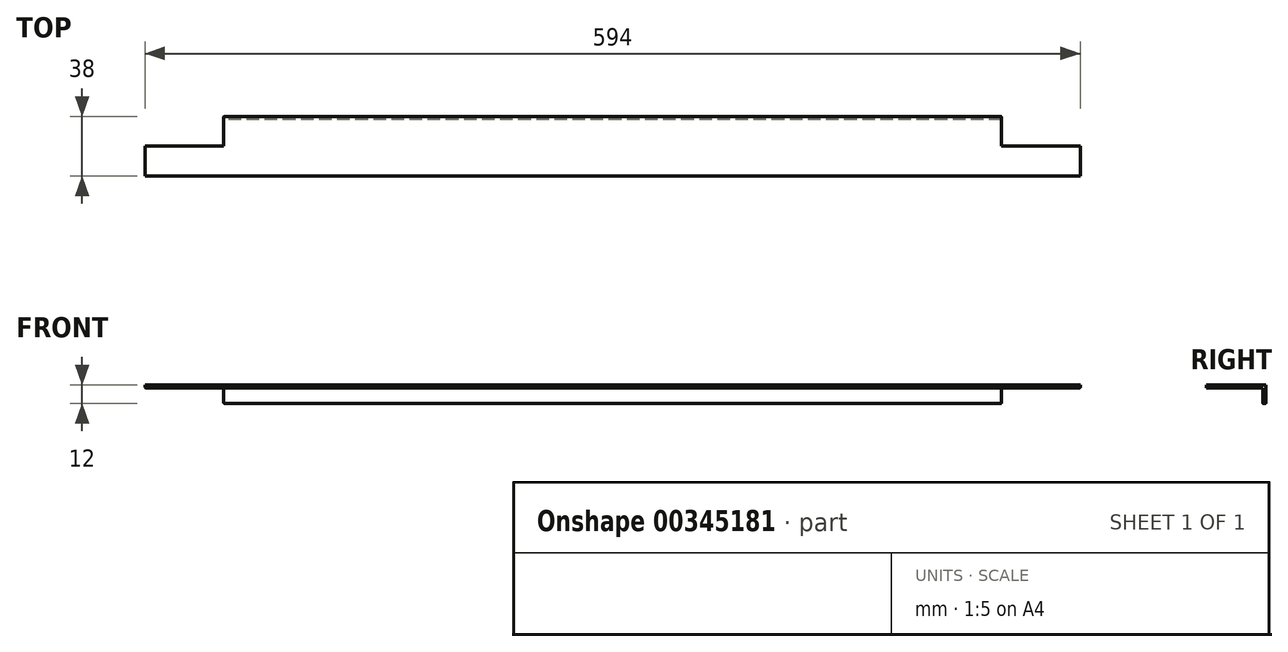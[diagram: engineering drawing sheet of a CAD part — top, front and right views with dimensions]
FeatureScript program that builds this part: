
annotation { "Feature Type Name" : "Feature", "Feature Type Description" : "" }
export const myFeature = defineFeature(function(context is Context, id is Id, definition is map)
    precondition{}
    {
        {
            var Q0;
            Q0=qCreatedBy(makeId("Front.planeOp"),FACE);
            var sketch = newSketch(context, id + "F0", { "sketchPlane" : qUnion([Q0])});
            skLineSegment(sketch, "E0.bottom", {"start": v(0, 0) * mm, "end": v(-51.96, 0) * mm});
            skLineSegment(sketch, "E0.top", {"start": v(0, 27.06) * mm, "end": v(-51.96, 27.06) * mm});
            skLineSegment(sketch, "E0.left", {"start": v(0, 0) * mm, "end": v(0, 27.06) * mm});
            skLineSegment(sketch, "E0.right", {"start": v(-51.96, 0) * mm, "end": v(-51.96, 27.06) * mm});
            skSolve(sketch);
        }
        {
            var Q0;
            Q0=makeQuery(id+"F0.imprint","IMPRINT",FACE,{"disambiguationData":[TD([[makeQuery(id+"F0.imprint","IMPRINT",EDGE,{"derivedFrom":sQuery(id+"F0.wireOp",EDGE,"E0.bottom")}),-1.0]])]});
            extrude(context, id + "F1", {"entities" : qUnion([Q0]), "oppositeDirection" : true, "depth" : 38 * mm});
        }
        {
            var Q0;
            Q0=makeQuery(id+"F1.opExtrude","SWEPT_FACE",FACE,{"disambiguationData":[OSD([sQuery(id+"F0.wireOp",EDGE,"E0.bottom")])]});
            extrude(context, id + "F2", {"entities" : qUnion([Q0]), "operationType" : NewBodyOperationType.INTERSECT, "oppositeDirection" : true, "depth" : 2 * mm});
        }
        {
            var Q0;
            Q0=makeQuery(id+"F1.opExtrude","SWEPT_FACE",FACE,{"disambiguationData":[OSD([sQuery(id+"F0.wireOp",EDGE,"E0.left")])]});
            extrude(context, id + "F3", {"entities" : qUnion([Q0]), "operationType" : NewBodyOperationType.ADD, "oppositeDirection" : true, "depth" : 594 * mm});
        }
        {
            var Q0;
            Q0=makeQuery(id+"F1.opExtrude","SWEPT_FACE",FACE,{"disambiguationData":[OSD([sQuery(id+"F0.wireOp",EDGE,"E0.left")])]});
            var sketch = newSketch(context, id + "F4", { "sketchPlane" : qUnion([Q0])});
            skLineSegment(sketch, "E1", {"start": v(19, 2) * mm, "end": v(19, 0) * mm});
            skSolve(sketch);
        }
        {
            var Q0;
            {var subQ0=sQuery(id+"F4.wireOp",EDGE,"E1");Q0=makeQuery(id+"F4.imprint","IMPRINT",FACE,{"disambiguationData":[TD([[makeQuery(id+"F4.imprint","IMPRINT",EDGE,{"derivedFrom":subQ0}),1.0]])]});}
            extrude(context, id + "F5", {"entities" : qUnion([Q0]), "operationType" : NewBodyOperationType.REMOVE, "oppositeDirection" : true, "depth" : 50 * mm});
        }
        {
            var Q0;
            Q0=makeQuery(id+"F3.opExtrude","CAP_FACE",FACE,{"disambiguationData":[OSD([sQuery(id+"F0.wireOp",EDGE,"E0.left")])],"isStart":false});
            var sketch = newSketch(context, id + "F6", { "sketchPlane" : qUnion([Q0])});
            skLineSegment(sketch, "E2", {"start": v(-19, 2) * mm, "end": v(-19, 0) * mm});
            skSolve(sketch);
        }
        {
            var Q0;
            {var subQ0=sQuery(id+"F6.wireOp",EDGE,"E2");Q0=makeQuery(id+"F6.imprint","IMPRINT",FACE,{"disambiguationData":[TD([[makeQuery(id+"F6.imprint","IMPRINT",EDGE,{"derivedFrom":subQ0}),-1.0]])]});}
            extrude(context, id + "F7", {"entities" : qUnion([Q0]), "operationType" : NewBodyOperationType.REMOVE, "oppositeDirection" : true, "depth" : 50 * mm});
        }
        {
            var Q0;
            {var subQ0=sQuery(id+"F0.wireOp",EDGE,"E0.left");var subQ1=sQuery(id+"F0.wireOp",EDGE,"E0.bottom");Q0=makeQuery(id+"F3.boolean.opBoolean","MERGE",FACE,{"derivedFrom":[makeQuery(id+"F1.opExtrude","SWEPT_FACE",FACE,{"disambiguationData":[OSD([subQ1])]}),makeQuery(id+"F3.opExtrude","SWEPT_FACE",FACE,{"disambiguationData":[OSD([subQ1,subQ0]),TDD([makeQuery(id+"F1.opExtrude","SWEPT_EDGE",EDGE,{"disambiguationData":[OSD([subQ1,subQ0])]})])]})]});}
            var sketch = newSketch(context, id + "F8", { "sketchPlane" : qUnion([Q0])});
            skLineSegment(sketch, "E3.bottom", {"start": v(-50, -38) * mm, "end": v(-544, -38) * mm});
            skLineSegment(sketch, "E3.top", {"start": v(-50, -28.5) * mm, "end": v(-544, -28.5) * mm});
            skLineSegment(sketch, "E3.left", {"start": v(-50, -38) * mm, "end": v(-50, -28.5) * mm});
            skLineSegment(sketch, "E3.right", {"start": v(-544, -38) * mm, "end": v(-544, -28.5) * mm});
            skSolve(sketch);
        }
        {
            var Q0;
            Q0=makeQuery(id+"F8.imprint","IMPRINT",FACE,{"disambiguationData":[TD([[makeQuery(id+"F8.imprint","IMPRINT",EDGE,{"derivedFrom":sQuery(id+"F8.wireOp",EDGE,"E3.bottom")}),-1.0]])]});
            extrude(context, id + "F9", {"entities" : qUnion([Q0]), "operationType" : NewBodyOperationType.ADD, "depth" : 10 * mm});
        }
        {
            var Q0;
            Q0=makeQuery(id+"F9.opExtrude","SWEPT_FACE",FACE,{"disambiguationData":[OSD([sQuery(id+"F8.wireOp",EDGE,"E3.top")])]});
            extrude(context, id + "F10", {"entities" : qUnion([Q0]), "operationType" : NewBodyOperationType.REMOVE, "oppositeDirection" : true, "depth" : 7.5 * mm});
        }
        {
            var Q0;
            {var subQ0=sQuery(id+"F0.wireOp",EDGE,"E0.left");var subQ1=sQuery(id+"F0.wireOp",EDGE,"E0.bottom");Q0=makeQuery(id+"F3.boolean.opBoolean","MERGE",EDGE,{"derivedFrom":[makeQuery(id+"F2.boolean.opBoolean","COPY",EDGE,{"derivedFrom":makeQuery(id+"F2.boolean.toolComplement.opBoolean","COPY",EDGE,{"derivedFrom":makeQuery(id+"F2.opExtrude","CAP_EDGE",EDGE,{"disambiguationData":[OSD([subQ1]),TDD([makeQuery(id+"F1.opExtrude","CAP_EDGE",EDGE,{"disambiguationData":[OSD([subQ1])],"isStart":false})])],"isStart":false})})}),makeQuery(id+"F3.opExtrude","SWEPT_EDGE",EDGE,{"disambiguationData":[OSD([subQ1,subQ0]),TDD([makeQuery(id+"F2.boolean.opBoolean","COPY",VERTEX,{"derivedFrom":makeQuery(id+"F2.boolean.toolComplement.opBoolean","COPY",VERTEX,{"derivedFrom":makeQuery(id+"F2.opExtrude","CAP_VERTEX",VERTEX,{"disambiguationData":[OSD([subQ1,subQ0]),TDD([makeQuery(id+"F1.opExtrude","CAP_VERTEX",VERTEX,{"disambiguationData":[OSD([subQ1,subQ0])],"isStart":false})])],"isStart":false})})})])]})]});}
            var Q1;
            Q1=makeQuery(id+"F9.boolean.opBoolean","MERGE",EDGE,{"derivedFrom":[makeQuery(id+"F7.boolean.opBoolean","COPY",EDGE,{"derivedFrom":makeQuery(id+"F7.opExtrude","CAP_EDGE",EDGE,{"disambiguationData":[OSD([sQuery(id+"F0.wireOp",EDGE,"E0.left")])],"isStart":false})}),makeQuery(id+"F9.opExtrude","SWEPT_EDGE",EDGE,{"disambiguationData":[OSD([sQuery(id+"F8.wireOp",EDGE,"E3.bottom"),sQuery(id+"F8.wireOp",EDGE,"E3.right")])]})]});
            var Q2;
            {var subQ0=sQuery(id+"F0.wireOp",EDGE,"E0.left");var subQ1=sQuery(id+"F0.wireOp",EDGE,"E0.bottom");var subQ2=makeQuery(id+"F3.opExtrude","CAP_EDGE",EDGE,{"disambiguationData":[OSD([subQ1,subQ0]),TDD([makeQuery(id+"F2.boolean.opBoolean","COPY",EDGE,{"derivedFrom":makeQuery(id+"F2.boolean.toolComplement.opBoolean","COPY",EDGE,{"derivedFrom":makeQuery(id+"F2.opExtrude","CAP_EDGE",EDGE,{"disambiguationData":[OSD([subQ1,subQ0])],"isStart":false})})})])],"isStart":false});Q2=makeQuery(id+"F7.boolean.opBoolean","COPY",EDGE,{"derivedFrom":makeQuery(id+"F7.opExtrude","CAP_EDGE",EDGE,{"disambiguationData":[OSD([subQ1,subQ0]),TDD([makeQuery(id+"F6.imprint","IMPRINT",EDGE,{"disambiguationData":[TD([[makeQuery(id+"F6.imprint","INTERSECT",VERTEX,{"derivedFrom":[subQ2,sQuery(id+"F6.wireOp",EDGE,"E2")]}),1.0]])],"derivedFrom":subQ2})])],"isStart":false})});}
            var Q3;
            {var subQ0=sQuery(id+"F8.wireOp",EDGE,"E3.right");var subQ1=sQuery(id+"F8.wireOp",EDGE,"E3.top");var subQ2=sQuery(id+"F0.wireOp",EDGE,"E0.left");var subQ3=sQuery(id+"F0.wireOp",EDGE,"E0.bottom");var subQ4=makeQuery(id+"F3.opExtrude","CAP_EDGE",EDGE,{"disambiguationData":[OSD([subQ3,subQ2]),TDD([makeQuery(id+"F1.opExtrude","SWEPT_EDGE",EDGE,{"disambiguationData":[OSD([subQ3,subQ2])]})])],"isStart":false});Q3=makeQuery(id+"F10.boolean.opBoolean","MERGE",EDGE,{"derivedFrom":[makeQuery(id+"F7.boolean.opBoolean","COPY",EDGE,{"derivedFrom":makeQuery(id+"F7.opExtrude","CAP_EDGE",EDGE,{"disambiguationData":[OSD([subQ3,subQ2]),TDD([makeQuery(id+"F6.imprint","IMPRINT",EDGE,{"disambiguationData":[TD([[makeQuery(id+"F6.imprint","INTERSECT",VERTEX,{"derivedFrom":[subQ4,sQuery(id+"F6.wireOp",EDGE,"E2")]}),1.0]])],"derivedFrom":subQ4})])],"isStart":false})}),makeQuery(id+"F10.opExtrude","SWEPT_EDGE",EDGE,{"disambiguationData":[OSD([subQ3,subQ2,subQ1,subQ0]),TDD([makeQuery(id+"F9.opExtrude","CAP_VERTEX",VERTEX,{"disambiguationData":[OSD([subQ3,subQ2,subQ1,subQ0])],"isStart":true})])]})]});}
            var Q4;
            Q4=makeQuery(id+"F10.boolean.opBoolean","COPY",EDGE,{"derivedFrom":makeQuery(id+"F10.opExtrude","CAP_EDGE",EDGE,{"disambiguationData":[OSD([sQuery(id+"F0.wireOp",EDGE,"E0.bottom"),sQuery(id+"F0.wireOp",EDGE,"E0.left"),sQuery(id+"F8.wireOp",EDGE,"E3.top"),sQuery(id+"F8.wireOp",EDGE,"E3.right")])],"isStart":false})});
            var Q5;
            {var subQ0=sQuery(id+"F0.wireOp",EDGE,"E0.left");var subQ1=sQuery(id+"F0.wireOp",EDGE,"E0.bottom");Q5=makeQuery(id+"F3.opExtrude","CAP_EDGE",EDGE,{"disambiguationData":[OSD([subQ1,subQ0]),TDD([makeQuery(id+"F2.boolean.opBoolean","COPY",EDGE,{"derivedFrom":makeQuery(id+"F2.boolean.toolComplement.opBoolean","COPY",EDGE,{"derivedFrom":makeQuery(id+"F2.opExtrude","CAP_EDGE",EDGE,{"disambiguationData":[OSD([subQ1,subQ0])],"isStart":false})})})])],"isStart":false});}
            var Q6;
            {var subQ0=sQuery(id+"F0.wireOp",EDGE,"E0.left");var subQ1=sQuery(id+"F0.wireOp",EDGE,"E0.bottom");Q6=makeQuery(id+"F3.opExtrude","CAP_EDGE",EDGE,{"disambiguationData":[OSD([subQ1,subQ0]),TDD([makeQuery(id+"F1.opExtrude","SWEPT_EDGE",EDGE,{"disambiguationData":[OSD([subQ1,subQ0])]})])],"isStart":false});}
            var Q7;
            {var subQ0=sQuery(id+"F6.wireOp",EDGE,"E2");var subQ1=sQuery(id+"F0.wireOp",EDGE,"E0.left");var subQ2=sQuery(id+"F0.wireOp",EDGE,"E0.bottom");Q7=makeQuery(id+"F7.boolean.opBoolean","COPY",EDGE,{"derivedFrom":makeQuery(id+"F7.opExtrude","SWEPT_EDGE",EDGE,{"disambiguationData":[OSD([subQ2,subQ1,subQ0]),TDD([makeQuery(id+"F6.imprint","INTERSECT",VERTEX,{"derivedFrom":[makeQuery(id+"F3.opExtrude","CAP_EDGE",EDGE,{"disambiguationData":[OSD([subQ2,subQ1]),TDD([makeQuery(id+"F1.opExtrude","SWEPT_EDGE",EDGE,{"disambiguationData":[OSD([subQ2,subQ1])]})])],"isStart":false}),subQ0]})])]})});}
            var Q8;
            {var subQ0=sQuery(id+"F6.wireOp",EDGE,"E2");var subQ1=sQuery(id+"F0.wireOp",EDGE,"E0.left");var subQ2=sQuery(id+"F0.wireOp",EDGE,"E0.bottom");Q8=makeQuery(id+"F7.boolean.opBoolean","COPY",EDGE,{"derivedFrom":makeQuery(id+"F7.opExtrude","SWEPT_EDGE",EDGE,{"disambiguationData":[OSD([subQ2,subQ1,subQ0]),TDD([makeQuery(id+"F6.imprint","INTERSECT",VERTEX,{"derivedFrom":[makeQuery(id+"F3.opExtrude","CAP_EDGE",EDGE,{"disambiguationData":[OSD([subQ2,subQ1]),TDD([makeQuery(id+"F2.boolean.opBoolean","COPY",EDGE,{"derivedFrom":makeQuery(id+"F2.boolean.toolComplement.opBoolean","COPY",EDGE,{"derivedFrom":makeQuery(id+"F2.opExtrude","CAP_EDGE",EDGE,{"disambiguationData":[OSD([subQ2,subQ1])],"isStart":false})})})])],"isStart":false}),subQ0]})])]})});}
            var Q9;
            Q9=makeQuery(id+"F9.opExtrude","CAP_EDGE",EDGE,{"disambiguationData":[OSD([sQuery(id+"F8.wireOp",EDGE,"E3.bottom")])],"isStart":false});
            var Q10;
            Q10=makeQuery(id+"F9.opExtrude","CAP_EDGE",EDGE,{"disambiguationData":[OSD([sQuery(id+"F8.wireOp",EDGE,"E3.right")])],"isStart":false});
            var Q11;
            Q11=makeQuery(id+"F9.opExtrude","CAP_EDGE",EDGE,{"disambiguationData":[OSD([sQuery(id+"F8.wireOp",EDGE,"E3.left")])],"isStart":false});
            var Q12;
            Q12=makeQuery(id+"F9.boolean.opBoolean","MERGE",EDGE,{"derivedFrom":[makeQuery(id+"F5.boolean.opBoolean","COPY",EDGE,{"derivedFrom":makeQuery(id+"F5.opExtrude","CAP_EDGE",EDGE,{"disambiguationData":[OSD([sQuery(id+"F0.wireOp",EDGE,"E0.left")])],"isStart":false})}),makeQuery(id+"F9.opExtrude","SWEPT_EDGE",EDGE,{"disambiguationData":[OSD([sQuery(id+"F8.wireOp",EDGE,"E3.bottom"),sQuery(id+"F8.wireOp",EDGE,"E3.left")])]})]});
            var Q13;
            Q13=makeQuery(id+"F10.boolean.opBoolean","COPY",EDGE,{"derivedFrom":makeQuery(id+"F10.opExtrude","CAP_EDGE",EDGE,{"disambiguationData":[OSD([sQuery(id+"F0.wireOp",EDGE,"E0.bottom"),sQuery(id+"F0.wireOp",EDGE,"E0.left"),sQuery(id+"F8.wireOp",EDGE,"E3.top"),sQuery(id+"F8.wireOp",EDGE,"E3.left")])],"isStart":false})});
            var Q14;
            {var subQ0=sQuery(id+"F8.wireOp",EDGE,"E3.left");var subQ1=sQuery(id+"F8.wireOp",EDGE,"E3.top");var subQ2=sQuery(id+"F0.wireOp",EDGE,"E0.left");var subQ3=sQuery(id+"F0.wireOp",EDGE,"E0.bottom");var subQ4=makeQuery(id+"F1.opExtrude","SWEPT_EDGE",EDGE,{"disambiguationData":[OSD([subQ3,subQ2])]});Q14=makeQuery(id+"F10.boolean.opBoolean","MERGE",EDGE,{"derivedFrom":[makeQuery(id+"F5.boolean.opBoolean","COPY",EDGE,{"derivedFrom":makeQuery(id+"F5.opExtrude","CAP_EDGE",EDGE,{"disambiguationData":[OSD([subQ3,subQ2]),TDD([makeQuery(id+"F4.imprint","IMPRINT",EDGE,{"disambiguationData":[TD([[makeQuery(id+"F4.imprint","INTERSECT",VERTEX,{"derivedFrom":[subQ4,makeQuery(id+"F1.opExtrude","CAP_EDGE",EDGE,{"disambiguationData":[OSD([subQ2])],"isStart":false})]}),-1.0]])],"derivedFrom":subQ4})])],"isStart":false})}),makeQuery(id+"F10.opExtrude","SWEPT_EDGE",EDGE,{"disambiguationData":[OSD([subQ3,subQ2,subQ1,subQ0]),TDD([makeQuery(id+"F9.opExtrude","CAP_VERTEX",VERTEX,{"disambiguationData":[OSD([subQ3,subQ2,subQ1,subQ0])],"isStart":true})])]})]});}
            var Q15;
            {var subQ0=sQuery(id+"F0.wireOp",EDGE,"E0.left");var subQ1=sQuery(id+"F0.wireOp",EDGE,"E0.bottom");var subQ2=makeQuery(id+"F2.boolean.opBoolean","COPY",EDGE,{"derivedFrom":makeQuery(id+"F2.boolean.toolComplement.opBoolean","COPY",EDGE,{"derivedFrom":makeQuery(id+"F2.opExtrude","CAP_EDGE",EDGE,{"disambiguationData":[OSD([subQ1,subQ0])],"isStart":false})})});Q15=makeQuery(id+"F5.boolean.opBoolean","COPY",EDGE,{"derivedFrom":makeQuery(id+"F5.opExtrude","CAP_EDGE",EDGE,{"disambiguationData":[OSD([subQ1,subQ0]),TDD([makeQuery(id+"F4.imprint","IMPRINT",EDGE,{"disambiguationData":[TD([[makeQuery(id+"F4.imprint","INTERSECT",VERTEX,{"derivedFrom":[subQ2,makeQuery(id+"F1.opExtrude","CAP_EDGE",EDGE,{"disambiguationData":[OSD([subQ0])],"isStart":false})]}),-1.0]])],"derivedFrom":subQ2})])],"isStart":false})});}
            var Q16;
            {var subQ0=sQuery(id+"F4.wireOp",EDGE,"E1");var subQ1=sQuery(id+"F0.wireOp",EDGE,"E0.left");var subQ2=sQuery(id+"F0.wireOp",EDGE,"E0.bottom");Q16=makeQuery(id+"F5.boolean.opBoolean","COPY",EDGE,{"derivedFrom":makeQuery(id+"F5.opExtrude","SWEPT_EDGE",EDGE,{"disambiguationData":[OSD([subQ2,subQ1,subQ0]),TDD([makeQuery(id+"F4.imprint","INTERSECT",VERTEX,{"derivedFrom":[makeQuery(id+"F2.boolean.opBoolean","COPY",EDGE,{"derivedFrom":makeQuery(id+"F2.boolean.toolComplement.opBoolean","COPY",EDGE,{"derivedFrom":makeQuery(id+"F2.opExtrude","CAP_EDGE",EDGE,{"disambiguationData":[OSD([subQ2,subQ1])],"isStart":false})})}),subQ0]})])]})});}
            var Q17;
            {var subQ0=sQuery(id+"F4.wireOp",EDGE,"E1");var subQ1=sQuery(id+"F0.wireOp",EDGE,"E0.left");var subQ2=sQuery(id+"F0.wireOp",EDGE,"E0.bottom");Q17=makeQuery(id+"F5.boolean.opBoolean","COPY",EDGE,{"derivedFrom":makeQuery(id+"F5.opExtrude","SWEPT_EDGE",EDGE,{"disambiguationData":[OSD([subQ2,subQ1,subQ0]),TDD([makeQuery(id+"F4.imprint","INTERSECT",VERTEX,{"derivedFrom":[makeQuery(id+"F1.opExtrude","SWEPT_EDGE",EDGE,{"disambiguationData":[OSD([subQ2,subQ1])]}),subQ0]})])]})});}
            var Q18;
            Q18=makeQuery(id+"F2.boolean.opBoolean","COPY",EDGE,{"derivedFrom":makeQuery(id+"F2.boolean.toolComplement.opBoolean","COPY",EDGE,{"derivedFrom":makeQuery(id+"F2.opExtrude","CAP_EDGE",EDGE,{"disambiguationData":[OSD([sQuery(id+"F0.wireOp",EDGE,"E0.bottom"),sQuery(id+"F0.wireOp",EDGE,"E0.left")])],"isStart":false})})});
            var Q19;
            Q19=makeQuery(id+"F1.opExtrude","SWEPT_EDGE",EDGE,{"disambiguationData":[OSD([sQuery(id+"F0.wireOp",EDGE,"E0.bottom"),sQuery(id+"F0.wireOp",EDGE,"E0.left")])]});
            fillet(context, id + "F11", {"entities" : qUnion([Q0, Q1, Q2, Q3, Q4, Q5, Q6, Q7, Q8, Q9, Q10, Q11, Q12, Q13, Q14, Q15, Q16, Q17, Q18, Q19]), "radius" : 0.5 * mm, "tangentPropagation" : true, "allowEdgeOverflow" : false});
        }
    });
